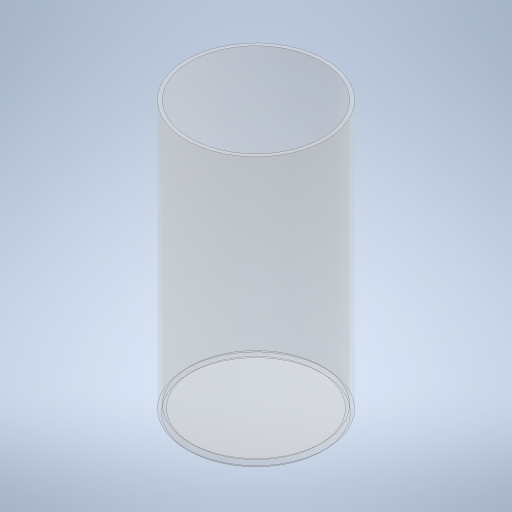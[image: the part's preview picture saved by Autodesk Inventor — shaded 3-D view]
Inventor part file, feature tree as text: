
AUTODESK INVENTOR PART (.ipt)
format: ipt  version: 2024 (Build 280153000, 153)  size: 283,136 bytes
history: native  units: mm
features: extrude x2, sketch x1, fillet x1
ambient origin geometry x8: Origin, YZ Plane, XZ Plane, XY Plane, X Axis, Y Axis, Z Axis, Center Point
bodies: Solide1 (feature_tree)
feature tree (4):
  sketch  "Esquisse1"
  extrude  "Extrusion1"  Depth=90.61mm
  extrude  "Extrusion2"  Depth=95.4mm
  fillet  "Congé1"  Radius=185.0mm
